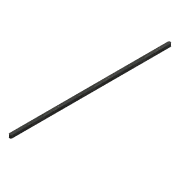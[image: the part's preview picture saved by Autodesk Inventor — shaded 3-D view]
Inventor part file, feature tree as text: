
AUTODESK INVENTOR PART (.ipt)
format: ipt  version: 2017 (Build 210142000, 142)  size: 82,944 bytes
history: native  units: mm
features: extrude x1, sketch x1
ambient origin geometry x8: Origin, YZ Plane, XZ Plane, XY Plane, X Axis, Y Axis, Z Axis, Center Point
bodies: Solid1 (feature_tree)
feature tree (2):
  extrude  "Extrusion1"  Depth=10.0mm
  sketch  "Sketch1"  dims[d0=550.0mm d1=10.0mm d2=2.0mm d3=2.0mm d4=10.0mm d5=0.0mm]
